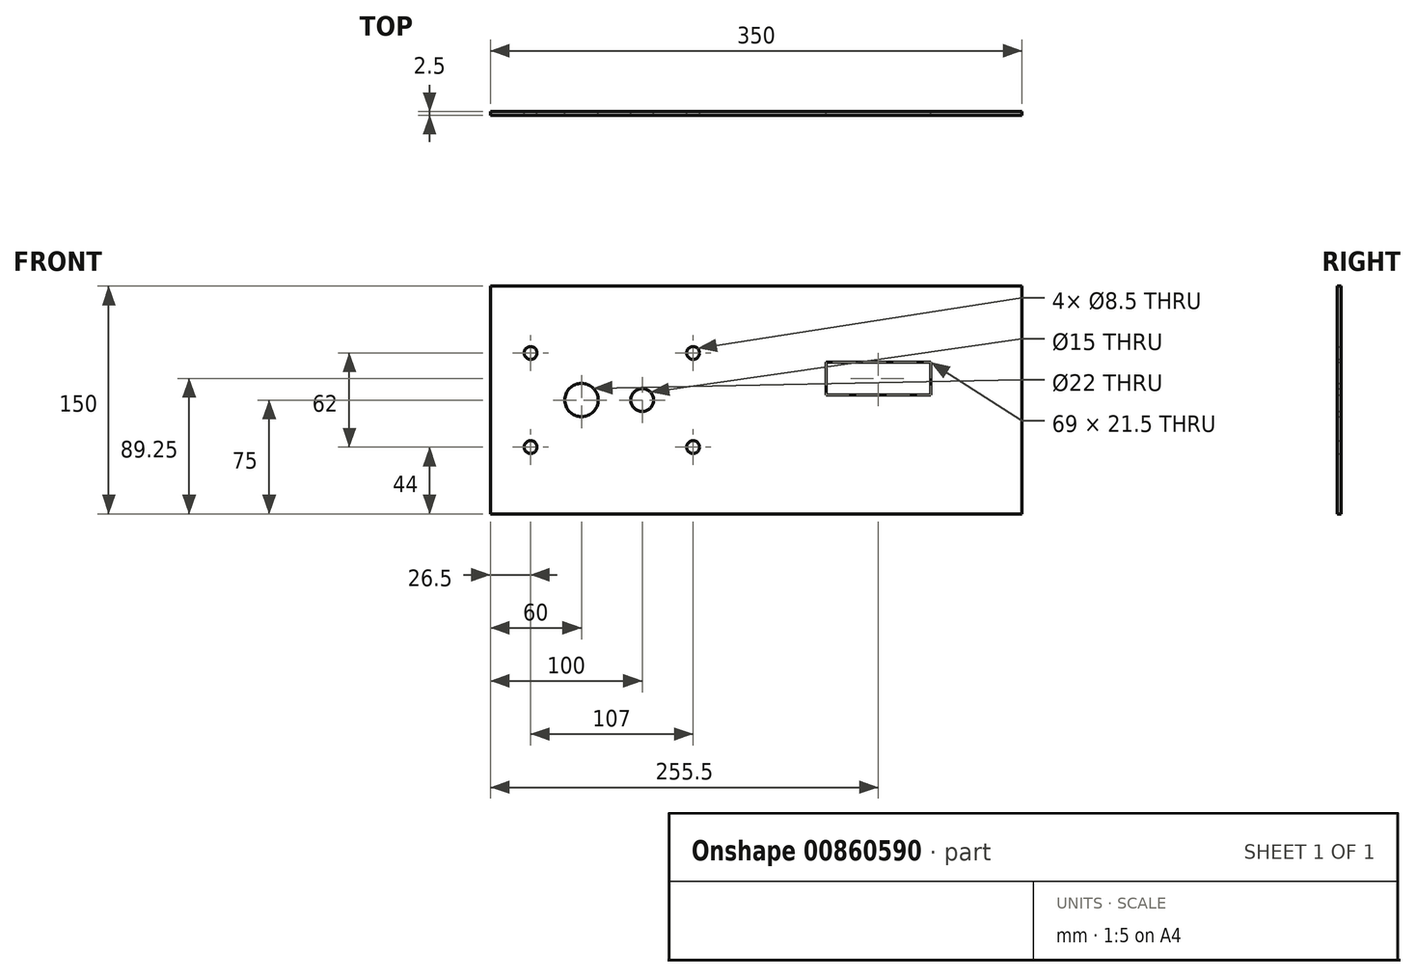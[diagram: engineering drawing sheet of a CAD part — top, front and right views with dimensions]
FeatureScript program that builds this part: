
annotation { "Feature Type Name" : "Feature", "Feature Type Description" : "" }
export const myFeature = defineFeature(function(context is Context, id is Id, definition is map)
    precondition{}
    {
        {
            var Q0;
            Q0=qCreatedBy(makeId("Front.planeOp"),FACE);
            var sketch = newSketch(context, id + "F0", { "sketchPlane" : qUnion([Q0])});
            skLineSegment(sketch, "E0.bottom", {"start": v(175, 75) * mm, "end": v(-175, 75) * mm});
            skLineSegment(sketch, "E0.top", {"start": v(175, -75) * mm, "end": v(-175, -75) * mm});
            skLineSegment(sketch, "E0.left", {"start": v(175, 75) * mm, "end": v(175, -75) * mm});
            skLineSegment(sketch, "E0.right", {"start": v(-175, 75) * mm, "end": v(-175, -75) * mm});
            skPoint(sketch, "E0.middle", {"position": v(0, 0) * mm});
            skCircle(sketch, "E1", {"center": v(-115, 0) * mm, "radius": 11 * mm});
            skCircle(sketch, "E2", {"center": v(-75, 0) * mm, "radius": 7.5 * mm});
            skCircle(sketch, "E3", {"center": v(-148.5, 31) * mm, "radius": 4.25 * mm});
            skCircle(sketch, "E4", {"center": v(-148.5, -31) * mm, "radius": 4.25 * mm});
            skCircle(sketch, "E5", {"center": v(-41.5, -31) * mm, "radius": 4.25 * mm});
            skCircle(sketch, "E6", {"center": v(-41.5, 31) * mm, "radius": 4.25 * mm});
            skLineSegment(sketch, "E7.bottom", {"start": v(46, 25) * mm, "end": v(115, 25) * mm});
            skLineSegment(sketch, "E7.top", {"start": v(46, 3.5) * mm, "end": v(115, 3.5) * mm});
            skLineSegment(sketch, "E7.left", {"start": v(46, 25) * mm, "end": v(46, 3.5) * mm});
            skLineSegment(sketch, "E7.right", {"start": v(115, 25) * mm, "end": v(115, 3.5) * mm});
            skSolve(sketch);
        }
        {
            var Q0;
            Q0 = qSketchRegion(id + "F0", true);
            extrude(context, id + "F1", {"entities" : qUnion([Q0]), "depth" : 2.5 * mm, "offsetDistance" : 25 * mm});
        }
    });
